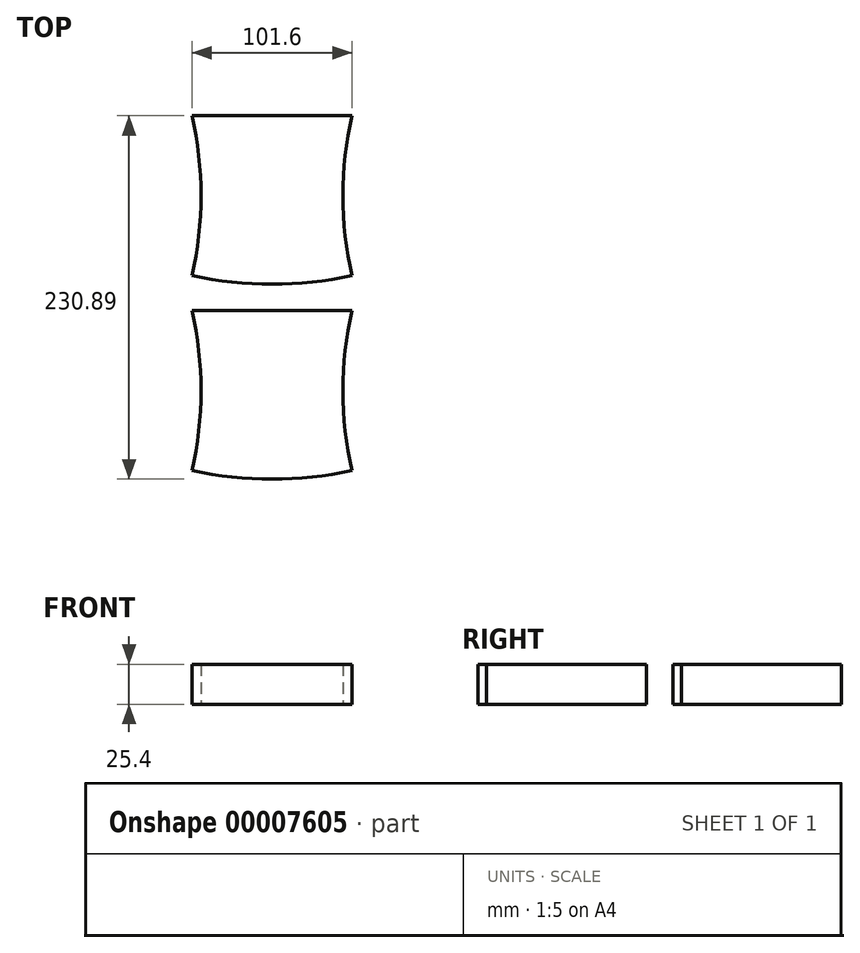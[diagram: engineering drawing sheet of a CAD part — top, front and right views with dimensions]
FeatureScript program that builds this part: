
annotation { "Feature Type Name" : "Feature", "Feature Type Description" : "" }
export const myFeature = defineFeature(function(context is Context, id is Id, definition is map)
    precondition{}
    {
        {
            var Q0;
            Q0=qCreatedBy(makeId("Top.planeOp"),FACE);
            var sketch = newSketch(context, id + "F0", { "sketchPlane" : qUnion([Q0])});
            skLineSegment(sketch, "E0", {"start": v(22.28, 45.22) * mm, "end": v(123.88, 45.22) * mm});
            skLineSegment(sketch, "E1", {"start": v(123.88, 45.22) * mm, "end": v(123.88, -56.38) * mm});
            skArc(sketch, "E2", {"start": v(123.88, 45.22) * mm, "mid": v(73.08, 50.66) * mm, "end": v(22.28, 45.22) * mm});
            skArc(sketch, "E3", {"start": v(123.88, 45.22) * mm, "mid": v(118.13, -5.58) * mm, "end": v(123.88, -56.38) * mm});
            skLineSegment(sketch, "E4", {"start": v(73.08, 45.22) * mm, "end": v(73.08, -56.38) * mm, "construction": true});
            skLineSegment(sketch, "E5", {"start": v(123.88, -5.58) * mm, "end": v(33.05, -5.58) * mm, "construction": true});
            skArc(sketch, "E6.0.MirrorCS", {"start": v(123.88, -56.38) * mm, "mid": v(73.08, -61.82) * mm, "end": v(22.28, -56.38) * mm});
            skArc(sketch, "E7.0.MirrorCS", {"start": v(22.28, 45.22) * mm, "mid": v(28.04, -5.58) * mm, "end": v(22.28, -56.38) * mm});
            skSolve(sketch);
        }
        {
            var Q0;
            Q0=makeQuery(id+"F0.imprint","IMPRINT",FACE,{"disambiguationData":[TD([[makeQuery(id+"F0.imprint","IMPRINT",EDGE,{"derivedFrom":sQuery(id+"F0.wireOp",EDGE,"E0")}),-1.0]])]});
            extrude(context, id + "F1", {"entities" : qUnion([Q0]), "depth" : 25.4 * mm});
        }
        {
            var Q0;
            Q0=qCreatedBy(makeId("Right.planeOp"),FACE);
            var Q1;
            Q1=makeQuery(id+"F1.opExtrude","CAP_VERTEX",VERTEX,{"disambiguationData":[OSD([sQuery(id+"F0.wireOp",EDGE,"E0"),sQuery(id+"F0.wireOp",EDGE,"E2"),sQuery(id+"F0.wireOp",EDGE,"E7.0.MirrorCS")])],"isStart":false});
            cPlane(context, id + "F2", {"entities" : qUnion([Q0, Q1]), "cplaneType" : CPlaneType.PLANE_POINT, "offset" : 152.4 * mm, "width" : 152.4 * mm, "height" : 152.4 * mm});
        }
        {
            var Q0;
            Q0=makeQuery(id+"F1.opExtrude","SWEPT_BODY",BODY,{"disambiguationData":[OSD([sQuery(id+"F0.wireOp",EDGE,"E0"),sQuery(id+"F0.wireOp",EDGE,"E3"),sQuery(id+"F0.wireOp",EDGE,"E6.0.MirrorCS"),sQuery(id+"F0.wireOp",EDGE,"E7.0.MirrorCS")])]});
            transform(context, id + "F3", {"entities" : qUnion([Q0]), "transformType" : TransformType.TRANSLATION_3D, "dx" : 0 * mm, "dy" : 123.84 * mm, "dz" : 0 * mm, "makeCopy" : true});
        }
    });
